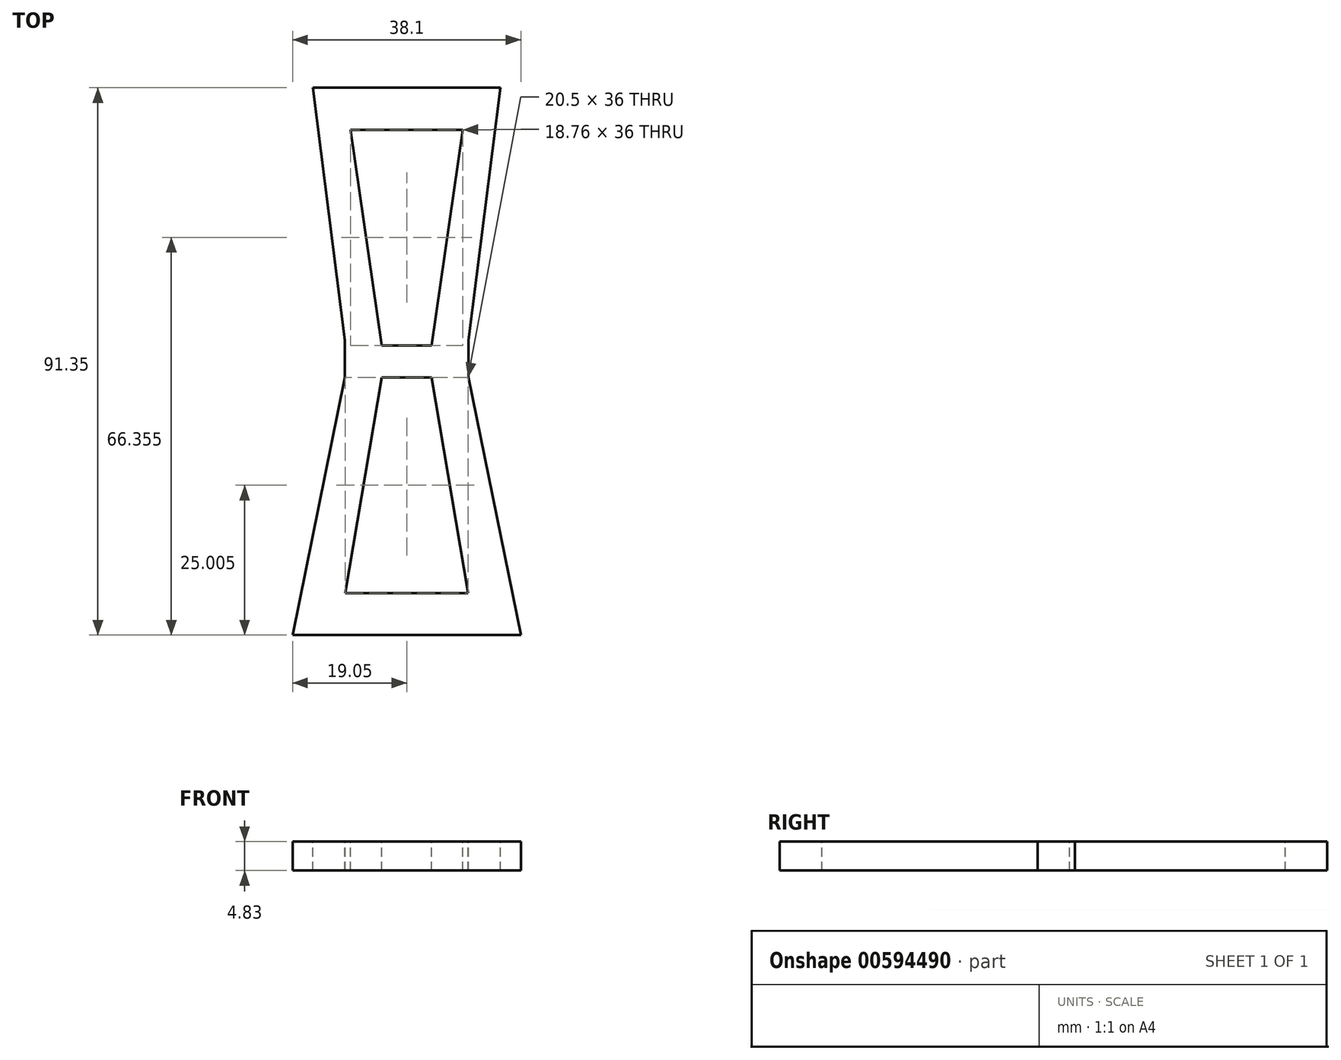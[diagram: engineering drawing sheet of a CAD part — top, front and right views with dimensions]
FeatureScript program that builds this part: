
annotation { "Feature Type Name" : "Feature", "Feature Type Description" : "" }
export const myFeature = defineFeature(function(context is Context, id is Id, definition is map)
    precondition{}
    {
        {
            var Q0;
            Q0=qCreatedBy(makeId("Top.planeOp"),FACE);
            var sketch = newSketch(context, id + "F0", { "sketchPlane" : qUnion([Q0])});
            skLineSegment(sketch, "E0", {"start": v(4.16, 2.68) * mm, "end": v(9.38, 38.68) * mm});
            skLineSegment(sketch, "E1", {"start": v(9.38, 38.68) * mm, "end": v(-9.38, 38.68) * mm});
            skLineSegment(sketch, "E2", {"start": v(-9.38, 38.68) * mm, "end": v(-4.16, 2.68) * mm});
            skLineSegment(sketch, "E3", {"start": v(-4.16, -2.68) * mm, "end": v(-10.25, -38.68) * mm});
            skLineSegment(sketch, "E4", {"start": v(-10.25, -38.68) * mm, "end": v(10.25, -38.68) * mm});
            skLineSegment(sketch, "E5", {"start": v(10.25, -38.68) * mm, "end": v(4.16, -2.68) * mm});
            skLineSegment(sketch, "E6", {"start": v(-15.67, 45.67) * mm, "end": v(-10.32, 3.55) * mm});
            skLineSegment(sketch, "E7", {"start": v(-10.32, 3.55) * mm, "end": v(-10.32, -2.68) * mm});
            skLineSegment(sketch, "E8", {"start": v(-10.32, -2.68) * mm, "end": v(-19.05, -45.68) * mm});
            skLineSegment(sketch, "E9", {"start": v(-19.05, -45.68) * mm, "end": v(19.05, -45.68) * mm});
            skLineSegment(sketch, "E10", {"start": v(19.05, -45.68) * mm, "end": v(10.32, -2.68) * mm});
            skLineSegment(sketch, "E11", {"start": v(10.32, -2.68) * mm, "end": v(10.32, 3.55) * mm});
            skLineSegment(sketch, "E12", {"start": v(10.32, 3.55) * mm, "end": v(15.67, 45.67) * mm});
            skLineSegment(sketch, "E13", {"start": v(15.67, 45.67) * mm, "end": v(-15.67, 45.67) * mm});
            skLineSegment(sketch, "E14", {"start": v(-4.16, 2.68) * mm, "end": v(4.16, 2.68) * mm});
            skLineSegment(sketch, "E15", {"start": v(-4.16, -2.68) * mm, "end": v(4.16, -2.68) * mm});
            skSolve(sketch);
        }
        {
            var Q0;
            Q0=makeQuery(id+"F0.imprint","IMPRINT",FACE,{"disambiguationData":[TD([[makeQuery(id+"F0.imprint","IMPRINT",EDGE,{"derivedFrom":sQuery(id+"F0.wireOp",EDGE,"E0")}),-1.0]])]});
            extrude(context, id + "F1", {"entities" : qUnion([Q0]), "oppositeDirection" : true, "depth" : 4.83 * mm, "offsetDistance" : 25.4 * mm});
        }
    });
